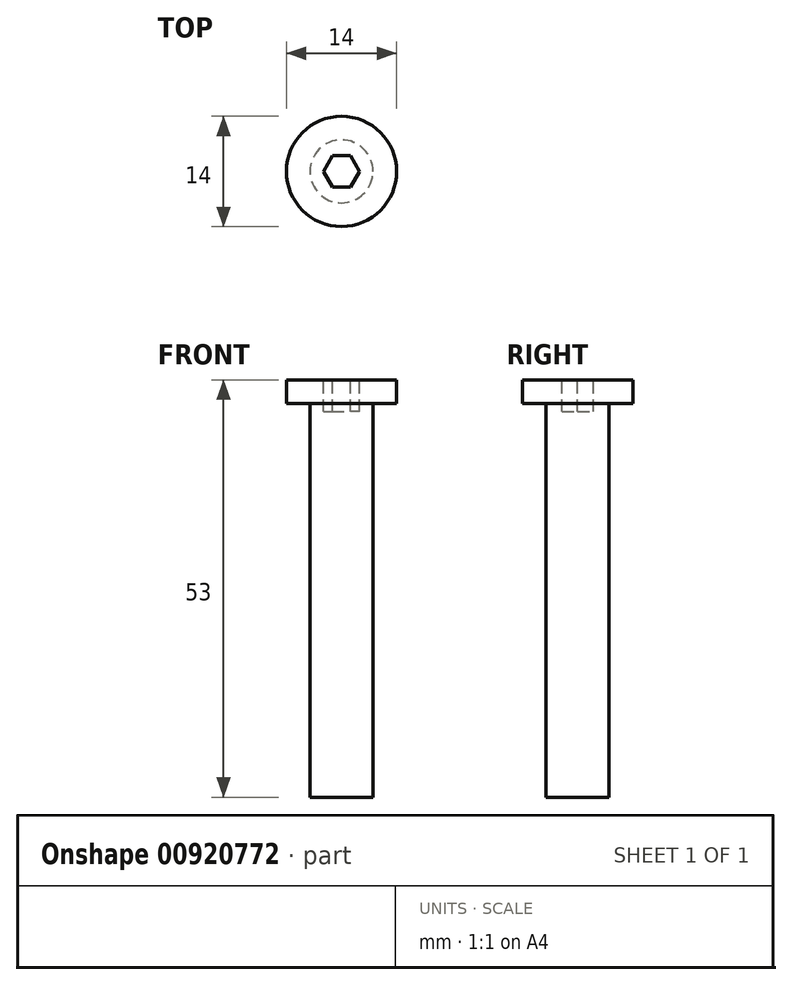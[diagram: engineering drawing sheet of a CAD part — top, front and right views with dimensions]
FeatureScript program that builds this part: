
annotation { "Feature Type Name" : "Feature", "Feature Type Description" : "" }
export const myFeature = defineFeature(function(context is Context, id is Id, definition is map)
    precondition{}
    {
        {
            var Q0;
            Q0=qCreatedBy(makeId("Top.planeOp"),FACE);
            var sketch = newSketch(context, id + "F0", { "sketchPlane" : qUnion([Q0])});
            skCircle(sketch, "E0", {"center": v(0, 0) * mm, "radius": 4 * mm});
            skSolve(sketch);
        }
        {
            var Q0;
            Q0=makeQuery(id+"F0.imprint","IMPRINT",FACE,{"disambiguationData":[TD([[makeQuery(id+"F0.imprint","IMPRINT",EDGE,{"derivedFrom":sQuery(id+"F0.wireOp",EDGE,"E0")}),1.0]])]});
            extrude(context, id + "F1", {"entities" : qUnion([Q0]), "depth" : 50 * mm, "offsetDistance" : 25 * mm});
        }
        {
            var Q0;
            Q0=makeQuery(id+"F1.opExtrude","CAP_FACE",FACE,{"disambiguationData":[OSD([sQuery(id+"F0.wireOp",EDGE,"E0")])],"isStart":false});
            var sketch = newSketch(context, id + "F2", { "sketchPlane" : qUnion([Q0])});
            skCircle(sketch, "E1", {"center": v(0, 0) * mm, "radius": 7 * mm});
            skSolve(sketch);
        }
        {
            var Q0;
            Q0=makeQuery(id+"F2.imprint","IMPRINT",FACE,{"disambiguationData":[TD([[makeQuery(id+"F2.imprint","IMPRINT",EDGE,{"derivedFrom":sQuery(id+"F2.wireOp",EDGE,"E1")}),1.0]])]});
            var Q1;
            Q1=makeQuery(id+"F2.imprint","IMPRINT",FACE,{"disambiguationData":[TD([[makeQuery(id+"F2.imprint","IMPRINT",EDGE,{"derivedFrom":makeQuery(id+"F1.opExtrude","CAP_EDGE",EDGE,{"disambiguationData":[OSD([sQuery(id+"F0.wireOp",EDGE,"E0")])],"isStart":false})}),1.0]])]});
            extrude(context, id + "F3", {"entities" : qUnion([Q0, Q1]), "operationType" : NewBodyOperationType.ADD, "depth" : 3 * mm, "offsetDistance" : 25 * mm});
        }
        {
            var Q0;
            Q0=makeQuery(id+"F3.opExtrude","CAP_FACE",FACE,{"disambiguationData":[OSD([sQuery(id+"F2.wireOp",EDGE,"E1")])],"isStart":false});
            var sketch = newSketch(context, id + "F4", { "sketchPlane" : qUnion([Q0])});
            skCircle(sketch, "E2.cCircle", {"center": v(0, 0) * mm, "radius": 2 * mm, "construction": true});
            skLineSegment(sketch, "E2.0", {"start": v(-1.15, 2) * mm, "end": v(1.15, 2) * mm});
            skLineSegment(sketch, "E2.1", {"start": v(1.15, 2) * mm, "end": v(2.3, 0) * mm});
            skLineSegment(sketch, "E2.2", {"start": v(2.3, 0) * mm, "end": v(1.15, -2) * mm});
            skLineSegment(sketch, "E2.3", {"start": v(1.15, -2) * mm, "end": v(-1.15, -2) * mm});
            skLineSegment(sketch, "E2.4", {"start": v(-1.15, -2) * mm, "end": v(-2.3, 0) * mm});
            skLineSegment(sketch, "E2.5", {"start": v(-2.3, 0) * mm, "end": v(-1.15, 2) * mm});
            skPoint(sketch, "E2.0.midPoint", {"position": v(0, 2) * mm});
            skSolve(sketch);
        }
        {
            var Q0;
            Q0=makeQuery(id+"F4.imprint","IMPRINT",FACE,{"disambiguationData":[TD([[makeQuery(id+"F4.imprint","IMPRINT",EDGE,{"derivedFrom":sQuery(id+"F4.wireOp",EDGE,"E2.0")}),-1.0]])]});
            extrude(context, id + "F5", {"entities" : qUnion([Q0]), "operationType" : NewBodyOperationType.REMOVE, "oppositeDirection" : true, "depth" : 4 * mm, "offsetDistance" : 25 * mm});
        }
    });
